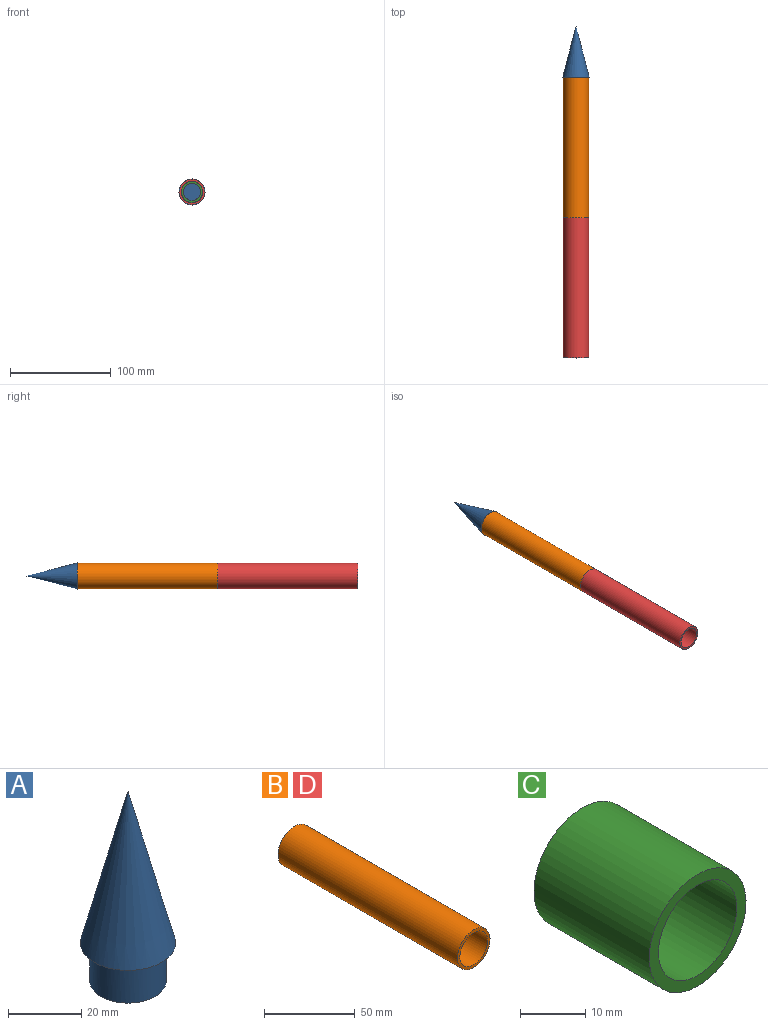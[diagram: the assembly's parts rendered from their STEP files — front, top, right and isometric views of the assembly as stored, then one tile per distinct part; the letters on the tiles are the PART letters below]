
ASSEMBLY  parts=4 mates=3
PART A: 4 faces, bbox 26x26x63.5 mm
  f0: cone r=13mm half-angle=14.4deg, axis (0,0,-1), area 2141.6mm2, adj f1
  f1: plane 26x26mm, normal (0,0,-1), area 187.2mm2, adj f0,f2
  f2: cylinder r=10.46mm len=20.92mm, axis (0,0,1), area 834.7mm2, adj f1,f3
  f3: plane 20.92x20.92mm, normal (0,0,-1), area 343.7mm2, adj f2
PART B: 4 faces, bbox 25.4x139.7x25.4 mm
  f0: cylinder r=12.7mm len=139.7mm, axis (0,1,0), area 11147.6mm2, adj f1,f2
  f1: plane 25.4x25.4mm, normal (0,-1,0), area 140.6mm2, adj f0,f3
  f2: plane 25.4x25.4mm, normal (0,1,0), area 140.6mm2, adj f0,f3
  f3: cylinder r=10.79mm len=139.7mm, axis (0,-1,0), area 9475.4mm2, adj f1,f2
PART C: 4 faces, bbox 21x25x21 mm
  f0: cylinder r=10.5mm len=25mm, axis (0,1,0), area 1649.3mm2, adj f1,f2
  f1: plane 21x21mm, normal (0,-1,0), area 119.4mm2, adj f0,f3
  f2: plane 21x21mm, normal (0,1,0), area 119.4mm2, adj f0,f3
  f3: cylinder r=8.5mm len=25mm, axis (0,-1,0), area 1335.2mm2, adj f1,f2
PART D: same geometry as B
PLACE A rot(axis=(-1,0,0),90deg) t=(8.28,206.05,-38.74)mm
PLACE B t=(-9.59,209.09,-38.74)mm
PLACE C t=(-9.59,81.89,-38.74)mm
PLACE D t=(-9.59,69.39,-38.74)mm
MATE fastened C.f0 <-> B.f0  axis (0,1,0) through (-9.59,69.39,-38.74)mm
MATE fastened B.f0 <-> D.f0  axis (0,-1,0) through (-9.59,69.39,-38.74)mm
MATE fastened A.f0 <-> B.f0  axis (0,-1,0) through (-9.59,209.09,-38.74)mm
